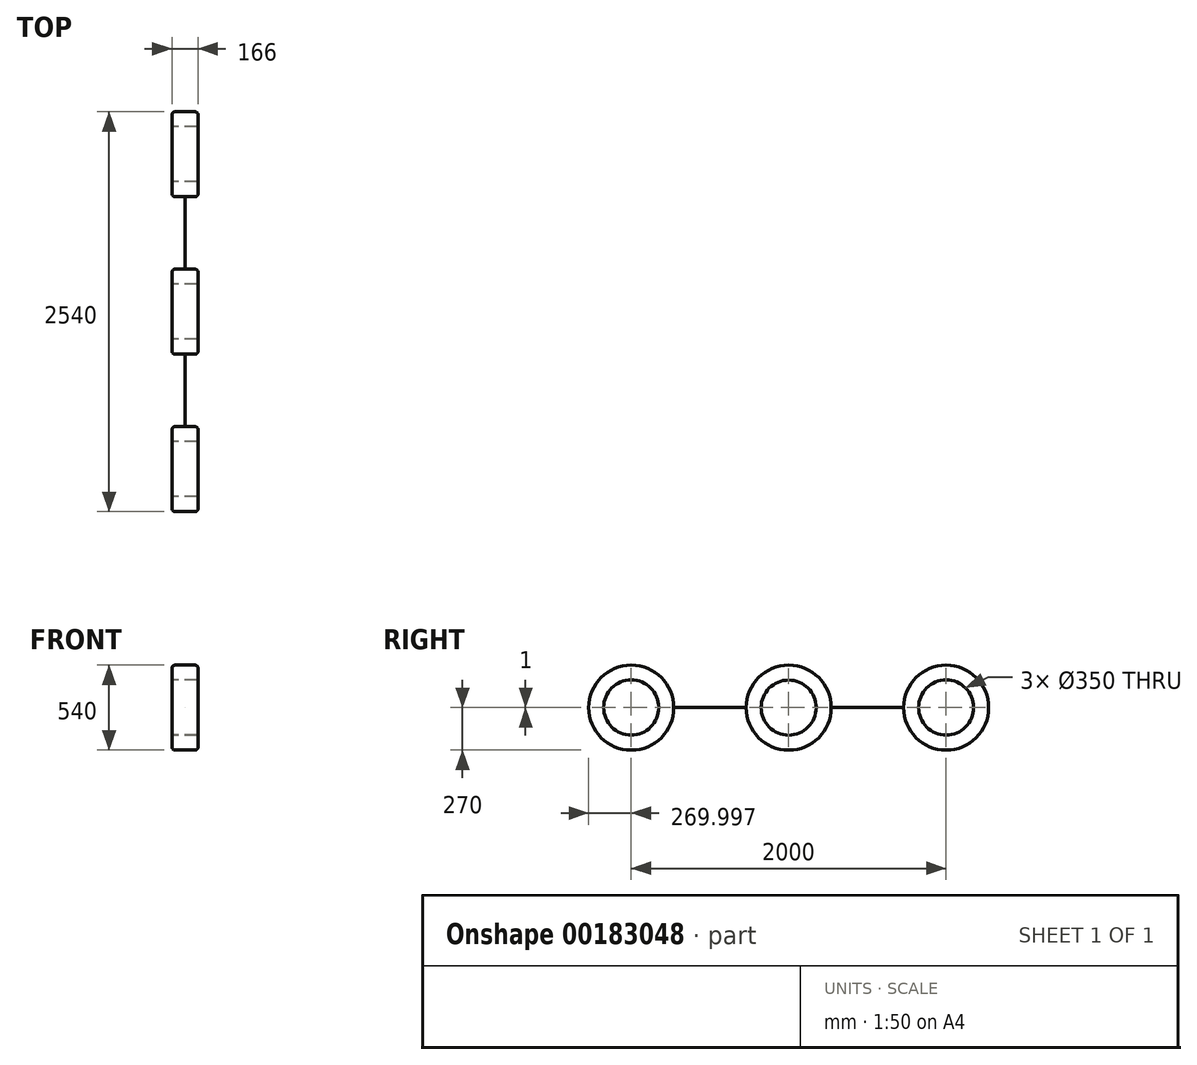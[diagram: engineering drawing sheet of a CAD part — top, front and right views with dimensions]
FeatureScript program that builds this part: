
annotation { "Feature Type Name" : "Feature", "Feature Type Description" : "" }
export const myFeature = defineFeature(function(context is Context, id is Id, definition is map)
    precondition{}
    {
        {
            var Q0;
            Q0=qCreatedBy(makeId("Right.planeOp"),FACE);
            var sketch = newSketch(context, id + "F0", { "sketchPlane" : qUnion([Q0])});
            skCircle(sketch, "E0", {"center": v(-534.92, 0) * mm, "radius": 270 * mm});
            skCircle(sketch, "E1", {"center": v(465.08, 0) * mm, "radius": 270 * mm});
            skCircle(sketch, "E2", {"center": v(1465.08, 0) * mm, "radius": 270 * mm});
            skLineSegment(sketch, "E3.bottom", {"start": v(-534.92, 0) * mm, "end": v(1465.08, 0) * mm});
            skLineSegment(sketch, "E3.top", {"start": v(-534.92, 1) * mm, "end": v(1465.08, 1) * mm});
            skLineSegment(sketch, "E3.left", {"start": v(-534.92, 0) * mm, "end": v(-534.92, 1) * mm});
            skLineSegment(sketch, "E3.right", {"start": v(1465.08, 0) * mm, "end": v(1465.08, 1) * mm});
            skCircle(sketch, "E4", {"center": v(-534.92, 1) * mm, "radius": 175 * mm});
            skCircle(sketch, "E5", {"center": v(465.08, 0) * mm, "radius": 175 * mm});
            skCircle(sketch, "E6", {"center": v(1465.08, 1) * mm, "radius": 175 * mm});
            skSolve(sketch);
        }
        {
            var Q0;
            {var subQ0=sQuery(id+"F0.wireOp",EDGE,"E3.bottom");var subQ1=sQuery(id+"F0.wireOp",EDGE,"E0");var subQ2=makeQuery(id+"F0.imprint","INTERSECT",VERTEX,{"derivedFrom":[subQ1,subQ0]});Q0=makeQuery(id+"F0.imprint","IMPRINT",FACE,{"disambiguationData":[TD([[makeQuery(id+"F0.imprint","IMPRINT",EDGE,{"disambiguationData":[TD([[subQ2,1.0]])],"derivedFrom":subQ1}),1.0]])]});}
            var Q1;
            {var subQ0=sQuery(id+"F0.wireOp",EDGE,"E3.top");var subQ1=sQuery(id+"F0.wireOp",EDGE,"E1");var subQ2=makeQuery(id+"F0.imprint","INTERSECT",VERTEX,{"disambiguationData":[OD(0.0)],"derivedFrom":[subQ1,subQ0]});Q1=makeQuery(id+"F0.imprint","IMPRINT",FACE,{"disambiguationData":[TD([[makeQuery(id+"F0.imprint","IMPRINT",EDGE,{"disambiguationData":[TD([[subQ2,-1.0]])],"derivedFrom":subQ1}),1.0]])]});}
            var Q2;
            {var subQ0=sQuery(id+"F0.wireOp",EDGE,"E3.bottom");var subQ1=sQuery(id+"F0.wireOp",EDGE,"E1");var subQ2=makeQuery(id+"F0.imprint","INTERSECT",VERTEX,{"disambiguationData":[OD(0.0)],"derivedFrom":[subQ1,subQ0]});Q2=makeQuery(id+"F0.imprint","IMPRINT",FACE,{"disambiguationData":[TD([[makeQuery(id+"F0.imprint","IMPRINT",EDGE,{"disambiguationData":[TD([[subQ2,1.0]])],"derivedFrom":subQ1}),1.0]])]});}
            var Q3;
            {var subQ0=sQuery(id+"F0.wireOp",EDGE,"E3.bottom");var subQ1=sQuery(id+"F0.wireOp",EDGE,"E2");var subQ2=makeQuery(id+"F0.imprint","INTERSECT",VERTEX,{"derivedFrom":[subQ1,subQ0]});Q3=makeQuery(id+"F0.imprint","IMPRINT",FACE,{"disambiguationData":[TD([[makeQuery(id+"F0.imprint","IMPRINT",EDGE,{"disambiguationData":[TD([[subQ2,-1.0]])],"derivedFrom":subQ1}),1.0]])]});}
            var Q4;
            {var subQ0=sQuery(id+"F0.wireOp",EDGE,"E3.top");var subQ1=sQuery(id+"F0.wireOp",EDGE,"E1");var subQ2=makeQuery(id+"F0.imprint","INTERSECT",VERTEX,{"disambiguationData":[OD(1.0)],"derivedFrom":[subQ1,subQ0]});Q4=makeQuery(id+"F0.imprint","IMPRINT",FACE,{"disambiguationData":[TD([[makeQuery(id+"F0.imprint","IMPRINT",EDGE,{"disambiguationData":[TD([[subQ2,-1.0]])],"derivedFrom":subQ1}),1.0]])]});}
            var Q5;
            {var subQ0=sQuery(id+"F0.wireOp",EDGE,"E3.top");var subQ1=sQuery(id+"F0.wireOp",EDGE,"E1");var subQ2=makeQuery(id+"F0.imprint","INTERSECT",VERTEX,{"disambiguationData":[OD(0.0)],"derivedFrom":[subQ1,subQ0]});Q5=makeQuery(id+"F0.imprint","IMPRINT",FACE,{"disambiguationData":[TD([[makeQuery(id+"F0.imprint","IMPRINT",EDGE,{"disambiguationData":[TD([[subQ2,1.0]])],"derivedFrom":subQ1}),1.0]])]});}
            var Q6;
            {var subQ0=sQuery(id+"F0.wireOp",EDGE,"E3.bottom");var subQ1=sQuery(id+"F0.wireOp",EDGE,"E2");var subQ2=makeQuery(id+"F0.imprint","INTERSECT",VERTEX,{"derivedFrom":[subQ1,subQ0]});Q6=makeQuery(id+"F0.imprint","IMPRINT",FACE,{"disambiguationData":[TD([[makeQuery(id+"F0.imprint","IMPRINT",EDGE,{"disambiguationData":[TD([[subQ2,1.0]])],"derivedFrom":subQ1}),1.0]])]});}
            var Q7;
            {var subQ0=sQuery(id+"F0.wireOp",EDGE,"E3.bottom");var subQ1=sQuery(id+"F0.wireOp",EDGE,"E0");var subQ2=makeQuery(id+"F0.imprint","INTERSECT",VERTEX,{"derivedFrom":[subQ1,subQ0]});Q7=makeQuery(id+"F0.imprint","IMPRINT",FACE,{"disambiguationData":[TD([[makeQuery(id+"F0.imprint","IMPRINT",EDGE,{"disambiguationData":[TD([[subQ2,-1.0]])],"derivedFrom":subQ1}),1.0]])]});}
            extrude(context, id + "F1", {"entities" : qUnion([Q0, Q1, Q2, Q3, Q4, Q5, Q6, Q7]), "endBound" : BoundingType.SYMMETRIC, "depth" : 166 * mm});
        }
        {
            var Q0;
            Q0=makeQuery(id+"F1.opExtrude","CAP_EDGE",EDGE,{"disambiguationData":[OSD([sQuery(id+"F0.wireOp",EDGE,"E0")])],"isStart":false});
            var Q1;
            Q1=makeQuery(id+"F1.opExtrude","CAP_EDGE",EDGE,{"disambiguationData":[OSD([sQuery(id+"F0.wireOp",EDGE,"E0")])],"isStart":true});
            var Q2;
            {var subQ0=sQuery(id+"F0.wireOp",EDGE,"E3.top");var subQ1=sQuery(id+"F0.wireOp",EDGE,"E1");Q2=makeQuery(id+"F1.opExtrude","CAP_EDGE",EDGE,{"disambiguationData":[OSD([subQ1]),TDD([makeQuery(id+"F0.imprint","IMPRINT",EDGE,{"disambiguationData":[TD([[makeQuery(id+"F0.imprint","INTERSECT",VERTEX,{"disambiguationData":[OD(0.0)],"derivedFrom":[subQ1,subQ0]}),-1.0]])],"derivedFrom":subQ1})])],"isStart":false});}
            var Q3;
            {var subQ0=sQuery(id+"F0.wireOp",EDGE,"E3.top");var subQ1=sQuery(id+"F0.wireOp",EDGE,"E1");Q3=makeQuery(id+"F1.opExtrude","CAP_EDGE",EDGE,{"disambiguationData":[OSD([subQ1]),TDD([makeQuery(id+"F0.imprint","IMPRINT",EDGE,{"disambiguationData":[TD([[makeQuery(id+"F0.imprint","INTERSECT",VERTEX,{"disambiguationData":[OD(0.0)],"derivedFrom":[subQ1,subQ0]}),-1.0]])],"derivedFrom":subQ1})])],"isStart":true});}
            var Q4;
            {var subQ0=sQuery(id+"F0.wireOp",EDGE,"E3.bottom");var subQ1=sQuery(id+"F0.wireOp",EDGE,"E1");Q4=makeQuery(id+"F1.opExtrude","CAP_EDGE",EDGE,{"disambiguationData":[OSD([subQ1]),TDD([makeQuery(id+"F0.imprint","IMPRINT",EDGE,{"disambiguationData":[TD([[makeQuery(id+"F0.imprint","INTERSECT",VERTEX,{"disambiguationData":[OD(0.0)],"derivedFrom":[subQ1,subQ0]}),1.0]])],"derivedFrom":subQ1})])],"isStart":false});}
            var Q5;
            Q5=makeQuery(id+"F1.opExtrude","CAP_EDGE",EDGE,{"disambiguationData":[OSD([sQuery(id+"F0.wireOp",EDGE,"E2")])],"isStart":false});
            var Q6;
            Q6=makeQuery(id+"F1.opExtrude","CAP_EDGE",EDGE,{"disambiguationData":[OSD([sQuery(id+"F0.wireOp",EDGE,"E2")])],"isStart":true});
            var Q7;
            {var subQ0=sQuery(id+"F0.wireOp",EDGE,"E3.bottom");var subQ1=sQuery(id+"F0.wireOp",EDGE,"E1");Q7=makeQuery(id+"F1.opExtrude","CAP_EDGE",EDGE,{"disambiguationData":[OSD([subQ1]),TDD([makeQuery(id+"F0.imprint","IMPRINT",EDGE,{"disambiguationData":[TD([[makeQuery(id+"F0.imprint","INTERSECT",VERTEX,{"disambiguationData":[OD(0.0)],"derivedFrom":[subQ1,subQ0]}),1.0]])],"derivedFrom":subQ1})])],"isStart":true});}
            fillet(context, id + "F2", {"entities" : qUnion([Q0, Q1, Q2, Q3, Q4, Q5, Q6, Q7]), "radius" : 20 * mm, "tangentPropagation" : true, "allowEdgeOverflow" : false});
        }
        {
            var Q0;
            Q0=qSketchRegion(id+"F0",true);
            extrude(context, id + "F3", {"entities" : qUnion([Q0]), "operationType" : NewBodyOperationType.ADD, "endBound" : BoundingType.SYMMETRIC, "depth" : 1 * mm});
        }
        {
            var Q0;
            Q0=makeQuery(id+"F1.opExtrude","CAP_EDGE",EDGE,{"disambiguationData":[OSD([sQuery(id+"F0.wireOp",EDGE,"E4")])],"isStart":false});
            var Q1;
            Q1=makeQuery(id+"F1.opExtrude","CAP_EDGE",EDGE,{"disambiguationData":[OSD([sQuery(id+"F0.wireOp",EDGE,"E4")])],"isStart":true});
            var Q2;
            Q2=makeQuery(id+"F1.opExtrude","CAP_EDGE",EDGE,{"disambiguationData":[OSD([sQuery(id+"F0.wireOp",EDGE,"E5")])],"isStart":false});
            var Q3;
            Q3=makeQuery(id+"F1.opExtrude","CAP_EDGE",EDGE,{"disambiguationData":[OSD([sQuery(id+"F0.wireOp",EDGE,"E5")])],"isStart":true});
            var Q4;
            Q4=makeQuery(id+"F1.opExtrude","CAP_EDGE",EDGE,{"disambiguationData":[OSD([sQuery(id+"F0.wireOp",EDGE,"E6")])],"isStart":false});
            var Q5;
            Q5=makeQuery(id+"F1.opExtrude","CAP_EDGE",EDGE,{"disambiguationData":[OSD([sQuery(id+"F0.wireOp",EDGE,"E6")])],"isStart":true});
            fillet(context, id + "F4", {"entities" : qUnion([Q0, Q1, Q2, Q3, Q4, Q5]), "radius" : 10 * mm, "tangentPropagation" : true, "allowEdgeOverflow" : false});
        }
    });
